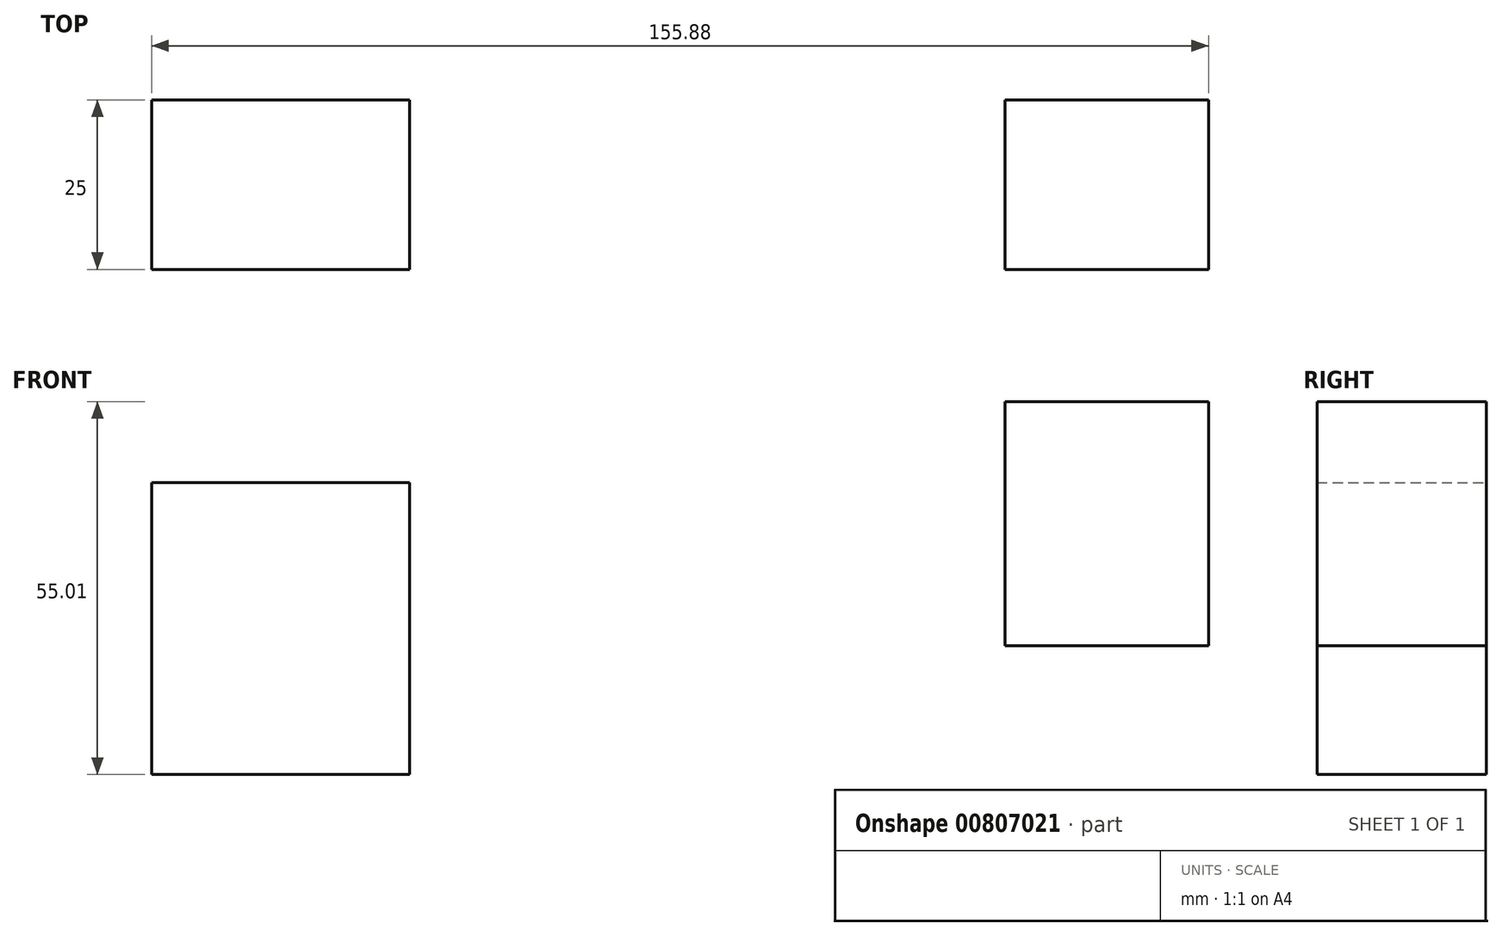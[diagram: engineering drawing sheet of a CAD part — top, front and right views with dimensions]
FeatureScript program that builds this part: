
annotation { "Feature Type Name" : "Feature", "Feature Type Description" : "" }
export const myFeature = defineFeature(function(context is Context, id is Id, definition is map)
    precondition{}
    {
        {
            var Q0;
            Q0=qCreatedBy(makeId("Front.planeOp"),FACE);
            var sketch = newSketch(context, id + "F0", { "sketchPlane" : qUnion([Q0])});
            skLineSegment(sketch, "E0.bottom", {"start": v(-102.97, 15.5) * mm, "end": v(-64.92, 15.5) * mm});
            skLineSegment(sketch, "E0.top", {"start": v(-102.97, 58.53) * mm, "end": v(-64.92, 58.53) * mm});
            skLineSegment(sketch, "E0.left", {"start": v(-102.97, 15.5) * mm, "end": v(-102.97, 58.53) * mm});
            skLineSegment(sketch, "E0.right", {"start": v(-64.92, 15.5) * mm, "end": v(-64.92, 58.53) * mm});
            skPoint(sketch, "E0.middle", {"position": v(-83.95, 37.02) * mm});
            skLineSegment(sketch, "E1.bottom", {"start": v(22.86, 34.47) * mm, "end": v(52.9, 34.47) * mm});
            skLineSegment(sketch, "E1.top", {"start": v(22.86, 70.51) * mm, "end": v(52.9, 70.51) * mm});
            skLineSegment(sketch, "E1.left", {"start": v(22.86, 34.47) * mm, "end": v(22.86, 70.51) * mm});
            skLineSegment(sketch, "E1.right", {"start": v(52.9, 34.47) * mm, "end": v(52.9, 70.51) * mm});
            skPoint(sketch, "E1.middle", {"position": v(37.88, 52.5) * mm});
            skSolve(sketch);
        }
        {
            var Q0;
            Q0 = qSketchRegion(id + "F0", true);
            extrude(context, id + "F1", {"entities" : qUnion([Q0]), "depth" : 25 * mm, "offsetDistance" : 25 * mm});
        }
    });
